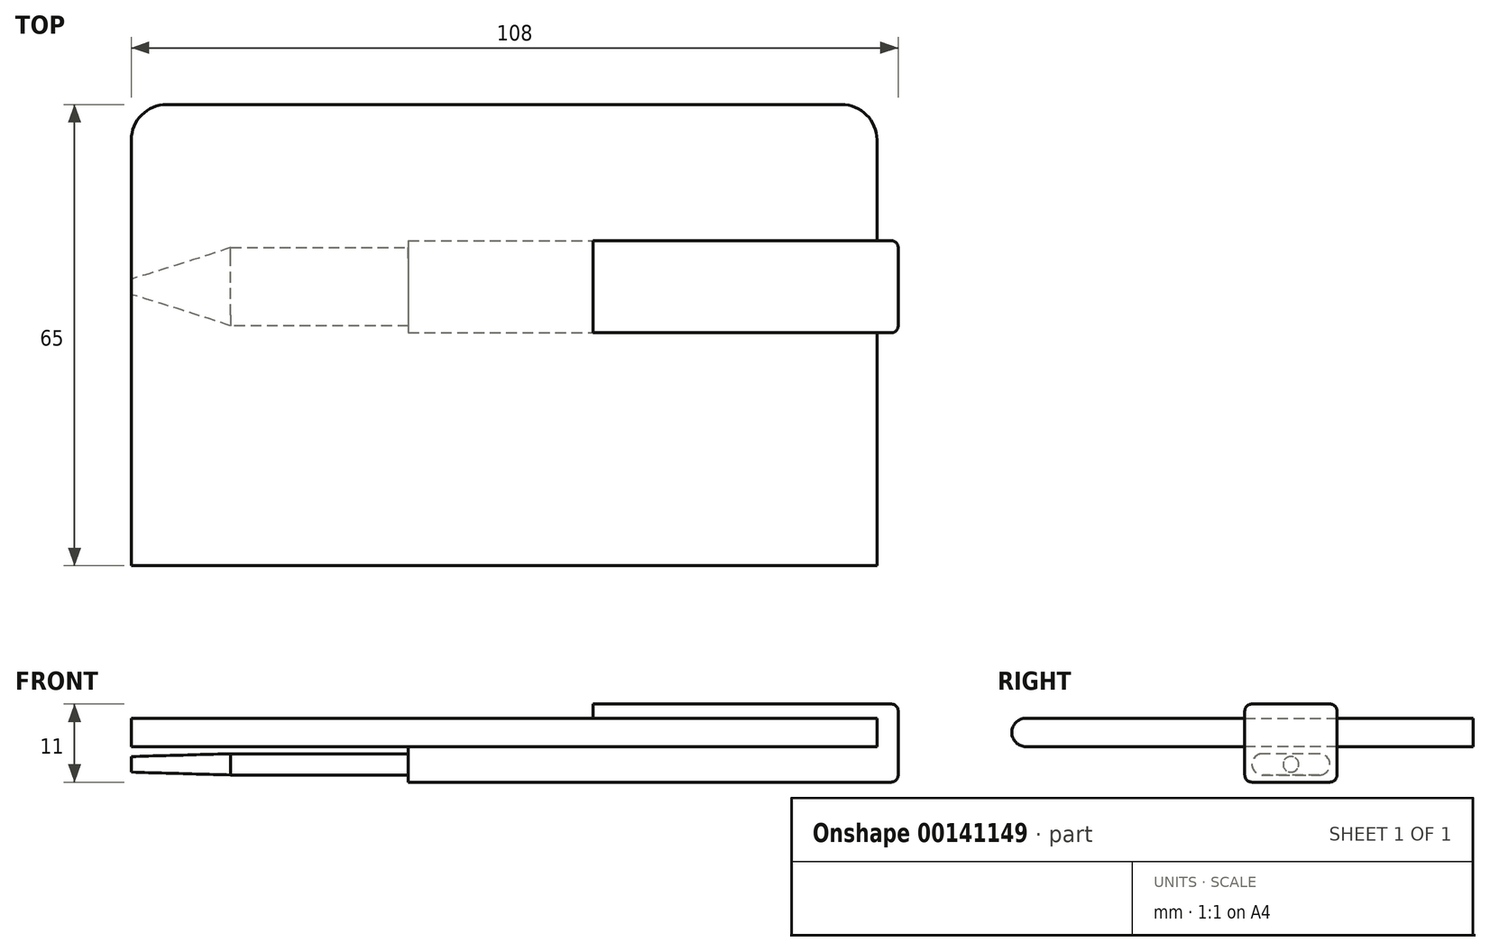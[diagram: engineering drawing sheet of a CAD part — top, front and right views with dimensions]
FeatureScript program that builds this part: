
annotation { "Feature Type Name" : "Feature", "Feature Type Description" : "" }
export const myFeature = defineFeature(function(context is Context, id is Id, definition is map)
    precondition{}
    {
        {
            var Q0;
            Q0=qCreatedBy(makeId("Top.planeOp"),FACE);
            var sketch = newSketch(context, id + "F0", { "sketchPlane" : qUnion([Q0])});
            skLineSegment(sketch, "E0.bottom", {"start": v(0, 0) * mm, "end": v(-105, 0) * mm});
            skLineSegment(sketch, "E0.top", {"start": v(-5, 65) * mm, "end": v(-100, 65) * mm});
            skLineSegment(sketch, "E0.left", {"start": v(0, 0) * mm, "end": v(0, 60) * mm});
            skLineSegment(sketch, "E0.right", {"start": v(-105, 0) * mm, "end": v(-105, 60) * mm});
            skPoint(sketch, "E1.visualSharp", {"position": v(-105, 65) * mm});
            skArc(sketch, "E1.filletArc", {"start": v(-100, 65) * mm, "mid": v(-103.54, 63.54) * mm, "end": v(-105, 60) * mm});
            skPoint(sketch, "E2.visualSharp", {"position": v(0, 65) * mm});
            skArc(sketch, "E2.filletArc", {"start": v(0, 60) * mm, "mid": v(-1.46, 63.54) * mm, "end": v(-5, 65) * mm});
            skSolve(sketch);
        }
        {
            var Q0;
            Q0=makeQuery(id+"F0.imprint","IMPRINT",FACE,{"disambiguationData":[TD([[makeQuery(id+"F0.imprint","IMPRINT",EDGE,{"derivedFrom":sQuery(id+"F0.wireOp",EDGE,"E0.bottom")}),-1.0]])]});
            extrude(context, id + "F1", {"entities" : qUnion([Q0]), "depth" : 4 * mm});
        }
        {
            var Q0;
            Q0=makeQuery(id+"F1.opExtrude","CAP_EDGE",EDGE,{"disambiguationData":[OSD([sQuery(id+"F0.wireOp",EDGE,"E0.bottom")])],"isStart":true});
            var Q1;
            Q1=makeQuery(id+"F1.opExtrude","CAP_EDGE",EDGE,{"disambiguationData":[OSD([sQuery(id+"F0.wireOp",EDGE,"E0.bottom")])],"isStart":false});
            fillet(context, id + "F2", {"entities" : qUnion([Q0, Q1]), "radius" : 2 * mm, "tangentPropagation" : true, "allowEdgeOverflow" : false});
        }
        {
            var Q0;
            Q0=qCreatedBy(makeId("Top.planeOp"),FACE);
            var sketch = newSketch(context, id + "F3", { "sketchPlane" : qUnion([Q0])});
            skLineSegment(sketch, "E3.bottom", {"start": v(-66, 45.81) * mm, "end": v(3, 45.81) * mm});
            skLineSegment(sketch, "E3.top", {"start": v(-66, 32.81) * mm, "end": v(3, 32.81) * mm});
            skLineSegment(sketch, "E3.left", {"start": v(-66, 45.81) * mm, "end": v(-66, 32.81) * mm});
            skLineSegment(sketch, "E3.right", {"start": v(3, 45.81) * mm, "end": v(3, 32.81) * mm});
            skSolve(sketch);
        }
        {
            var Q0;
            Q0 = qSketchRegion(id + "F3", true);
            extrude(context, id + "F4", {"entities" : qUnion([Q0]), "oppositeDirection" : true, "depth" : 5 * mm});
        }
        {
            var Q0;
            Q0=makeQuery(id+"F4.opExtrude","CAP_FACE",FACE,{"disambiguationData":[OSD([sQuery(id+"F3.wireOp",EDGE,"E3.bottom"),sQuery(id+"F3.wireOp",EDGE,"E3.top"),sQuery(id+"F3.wireOp",EDGE,"E3.left"),sQuery(id+"F3.wireOp",EDGE,"E3.right")])],"isStart":true});
            var sketch = newSketch(context, id + "F5", { "sketchPlane" : qUnion([Q0])});
            skLineSegment(sketch, "E4.bottom", {"start": v(3, 45.81) * mm, "end": v(0, 45.81) * mm});
            skLineSegment(sketch, "E4.top", {"start": v(3, 32.81) * mm, "end": v(0, 32.81) * mm});
            skLineSegment(sketch, "E4.left", {"start": v(3, 45.81) * mm, "end": v(3, 32.81) * mm});
            skLineSegment(sketch, "E4.right", {"start": v(0, 45.81) * mm, "end": v(0, 32.81) * mm});
            skSolve(sketch);
        }
        {
            var Q0;
            Q0 = qSketchRegion(id + "F5", true);
            extrude(context, id + "F6", {"entities" : qUnion([Q0]), "operationType" : NewBodyOperationType.ADD, "depth" : 6 * mm});
        }
        {
            var Q0;
            Q0=makeQuery(id+"F6.opExtrude","SWEPT_FACE",FACE,{"disambiguationData":[OSD([sQuery(id+"F5.wireOp",EDGE,"E4.right")])]});
            var sketch = newSketch(context, id + "F7", { "sketchPlane" : qUnion([Q0])});
            skLineSegment(sketch, "E5.bottom", {"start": v(-32.81, 6) * mm, "end": v(-45.81, 6) * mm});
            skLineSegment(sketch, "E5.top", {"start": v(-32.81, 4) * mm, "end": v(-45.81, 4) * mm});
            skLineSegment(sketch, "E5.left", {"start": v(-32.81, 6) * mm, "end": v(-32.81, 4) * mm});
            skLineSegment(sketch, "E5.right", {"start": v(-45.81, 6) * mm, "end": v(-45.81, 4) * mm});
            skSolve(sketch);
        }
        {
            var Q0;
            Q0 = qSketchRegion(id + "F7", true);
            extrude(context, id + "F8", {"entities" : qUnion([Q0]), "operationType" : NewBodyOperationType.ADD, "depth" : 40 * mm});
        }
        {
            var Q0;
            Q0=makeQuery(id+"F4.opExtrude","CAP_EDGE",EDGE,{"disambiguationData":[OSD([sQuery(id+"F3.wireOp",EDGE,"E3.bottom")])],"isStart":true});
            var Q1;
            Q1=makeQuery(id+"F4.opExtrude","CAP_EDGE",EDGE,{"disambiguationData":[OSD([sQuery(id+"F3.wireOp",EDGE,"E3.top")])],"isStart":true});
            var Q2;
            Q2=makeQuery(id+"F4.opExtrude","CAP_EDGE",EDGE,{"disambiguationData":[OSD([sQuery(id+"F3.wireOp",EDGE,"E3.top")])],"isStart":false});
            var Q3;
            Q3=makeQuery(id+"F6.opExtrude","CAP_EDGE",EDGE,{"disambiguationData":[OSD([sQuery(id+"F5.wireOp",EDGE,"E4.left")])],"isStart":false});
            var Q4;
            Q4=makeQuery(id+"F4.opExtrude","CAP_EDGE",EDGE,{"disambiguationData":[OSD([sQuery(id+"F3.wireOp",EDGE,"E3.right")])],"isStart":false});
            var Q5;
            Q5=makeQuery(id+"F6.boolean.opBoolean","MERGE",EDGE,{"derivedFrom":[makeQuery(id+"F4.opExtrude","SWEPT_EDGE",EDGE,{"disambiguationData":[OSD([sQuery(id+"F3.wireOp",EDGE,"E3.top"),sQuery(id+"F3.wireOp",EDGE,"E3.right")])]}),makeQuery(id+"F6.opExtrude","SWEPT_EDGE",EDGE,{"disambiguationData":[OSD([sQuery(id+"F5.wireOp",EDGE,"E4.top"),sQuery(id+"F5.wireOp",EDGE,"E4.left")])]})]});
            var Q6;
            Q6=makeQuery(id+"F6.boolean.opBoolean","MERGE",EDGE,{"derivedFrom":[makeQuery(id+"F4.opExtrude","SWEPT_EDGE",EDGE,{"disambiguationData":[OSD([sQuery(id+"F3.wireOp",EDGE,"E3.bottom"),sQuery(id+"F3.wireOp",EDGE,"E3.right")])]}),makeQuery(id+"F6.opExtrude","SWEPT_EDGE",EDGE,{"disambiguationData":[OSD([sQuery(id+"F5.wireOp",EDGE,"E4.bottom"),sQuery(id+"F5.wireOp",EDGE,"E4.left")])]})]});
            var Q7;
            Q7=makeQuery(id+"F8.boolean.opBoolean","MERGE",EDGE,{"derivedFrom":[makeQuery(id+"F6.opExtrude","CAP_EDGE",EDGE,{"disambiguationData":[OSD([sQuery(id+"F5.wireOp",EDGE,"E4.top")])],"isStart":false}),makeQuery(id+"F8.opExtrude","SWEPT_EDGE",EDGE,{"disambiguationData":[OSD([sQuery(id+"F7.wireOp",EDGE,"E5.bottom"),sQuery(id+"F7.wireOp",EDGE,"E5.left")])]})]});
            var Q8;
            Q8=makeQuery(id+"F8.boolean.opBoolean","MERGE",EDGE,{"derivedFrom":[makeQuery(id+"F6.opExtrude","CAP_EDGE",EDGE,{"disambiguationData":[OSD([sQuery(id+"F5.wireOp",EDGE,"E4.bottom")])],"isStart":false}),makeQuery(id+"F8.opExtrude","SWEPT_EDGE",EDGE,{"disambiguationData":[OSD([sQuery(id+"F7.wireOp",EDGE,"E5.bottom"),sQuery(id+"F7.wireOp",EDGE,"E5.right")])]})]});
            var Q9;
            Q9=makeQuery(id+"F4.opExtrude","CAP_EDGE",EDGE,{"disambiguationData":[OSD([sQuery(id+"F3.wireOp",EDGE,"E3.bottom")])],"isStart":false});
            fillet(context, id + "F9", {"entities" : qUnion([Q0, Q1, Q2, Q3, Q4, Q5, Q6, Q7, Q8, Q9]), "radius" : 1 * mm, "tangentPropagation" : true, "allowEdgeOverflow" : false});
        }
        {
            var Q0;
            Q0=makeQuery(id+"F1.opExtrude","SWEPT_FACE",FACE,{"disambiguationData":[OSD([sQuery(id+"F0.wireOp",EDGE,"E0.right")])]});
            var sketch = newSketch(context, id + "F10", { "sketchPlane" : qUnion([Q0])});
            skCircle(sketch, "E6", {"center": v(-39.31, -2.5) * mm, "radius": 1.1 * mm});
            skLineSegment(sketch, "E7", {"start": v(-39.31, -5) * mm, "end": v(-39.31, 0) * mm, "construction": true});
            skSolve(sketch);
        }
        {
            var Q0;
            Q0=makeQuery(id+"F4.opExtrude","SWEPT_FACE",FACE,{"disambiguationData":[OSD([sQuery(id+"F3.wireOp",EDGE,"E3.left")])]});
            var sketch = newSketch(context, id + "F11", { "sketchPlane" : qUnion([Q0])});
            skLineSegment(sketch, "E8.bottom", {"start": v(-44.81, -4) * mm, "end": v(-33.81, -4) * mm});
            skLineSegment(sketch, "E8.top", {"start": v(-44.81, -1) * mm, "end": v(-33.81, -1) * mm});
            skLineSegment(sketch, "E8.left", {"start": v(-44.81, -4) * mm, "end": v(-44.81, -1) * mm});
            skLineSegment(sketch, "E8.right", {"start": v(-33.81, -4) * mm, "end": v(-33.81, -1) * mm});
            skSolve(sketch);
        }
        {
            var Q0;
            Q0 = qSketchRegion(id + "F11", true);
            extrude(context, id + "F12", {"entities" : qUnion([Q0]), "operationType" : NewBodyOperationType.ADD, "depth" : 25 * mm});
        }
        {
            var Q0;
            Q0=makeQuery(id+"F12.opExtrude","SWEPT_EDGE",EDGE,{"disambiguationData":[OSD([sQuery(id+"F11.wireOp",EDGE,"E8.top"),sQuery(id+"F11.wireOp",EDGE,"E8.left")])]});
            var Q1;
            Q1=makeQuery(id+"F12.opExtrude","SWEPT_EDGE",EDGE,{"disambiguationData":[OSD([sQuery(id+"F11.wireOp",EDGE,"E8.bottom"),sQuery(id+"F11.wireOp",EDGE,"E8.left")])]});
            var Q2;
            Q2=makeQuery(id+"F12.opExtrude","SWEPT_EDGE",EDGE,{"disambiguationData":[OSD([sQuery(id+"F11.wireOp",EDGE,"E8.top"),sQuery(id+"F11.wireOp",EDGE,"E8.right")])]});
            var Q3;
            Q3=makeQuery(id+"F12.opExtrude","SWEPT_EDGE",EDGE,{"disambiguationData":[OSD([sQuery(id+"F11.wireOp",EDGE,"E8.bottom"),sQuery(id+"F11.wireOp",EDGE,"E8.right")])]});
            fillet(context, id + "F13", {"entities" : qUnion([Q0, Q1, Q2, Q3]), "radius" : 1.5 * mm, "tangentPropagation" : true, "allowEdgeOverflow" : false});
        }
        {
            var Q1;
            Q1=makeQuery(id+"F12.opExtrude","CAP_FACE",FACE,{"disambiguationData":[OSD([sQuery(id+"F11.wireOp",EDGE,"E8.bottom"),sQuery(id+"F11.wireOp",EDGE,"E8.top"),sQuery(id+"F11.wireOp",EDGE,"E8.left"),sQuery(id+"F11.wireOp",EDGE,"E8.right")])],"isStart":false});
            var Q2;
            Q2=makeQuery(id+"F10.imprint","IMPRINT",FACE,{"disambiguationData":[TD([[makeQuery(id+"F10.imprint","IMPRINT",EDGE,{"derivedFrom":sQuery(id+"F10.wireOp",EDGE,"E6")}),1.0]])]});
            loft(context, id + "F14", {"operationType" : NewBodyOperationType.ADD, "sheetProfilesArray" : [{ "sheetProfileEntities" : qUnion([Q1]) }, { "sheetProfileEntities" : qUnion([Q2]) }]});
        }
    });
